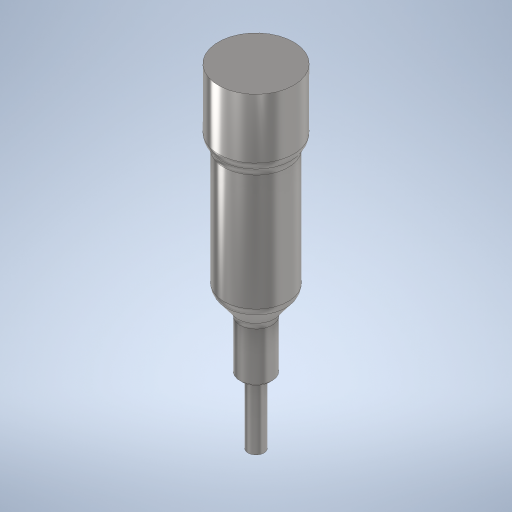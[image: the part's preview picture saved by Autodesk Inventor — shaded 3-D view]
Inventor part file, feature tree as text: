
AUTODESK INVENTOR PART (.ipt)
format: ipt  version: 2024.3 (Build 283343000, 343)  size: 280,576 bytes
history: native  units: mm
features: sketch x5, extrude x4, fillet x3, revolve x1, chamfer x1, other x1
ambient origin geometry x8: Origin, YZ Plane, XZ Plane, XY Plane, X Axis, Y Axis, Z Axis, Center Point
bodies: Solido1 (feature_tree)
feature tree (15):
  extrude  "Estrusione1"  Depth=0.07mm
  extrude  "Estrusione2"  Depth=0.06mm TaperAngle=0.0deg
  revolve  "Rivoluzione1"
  extrude  "Estrusione3"  Depth=0.06mm
  extrude  "Estrusione4"  Depth=0.12mm TaperAngle=0.0deg
  fillet  "Raccordo1"  Radius=0.02mm
  chamfer  "Smusso1"  Distance=0.015mm
  fillet  "Raccordo2"  [1 undecoded]
  fillet  "Raccordo3"  Radius=0.05mm
  sketch  "Schizzo1"
  sketch  "Schizzo2"
  sketch  "Schizzo3"
  other  "Linea chiusa proiettata1"
  sketch  "Schizzo4"
  sketch  "Schizzo5"
note: 1 required parameter value undecoded (feature->parameter linkage not recoverable at this tier; creation-order binding heuristic only, values carry confidence <= 0.55)
